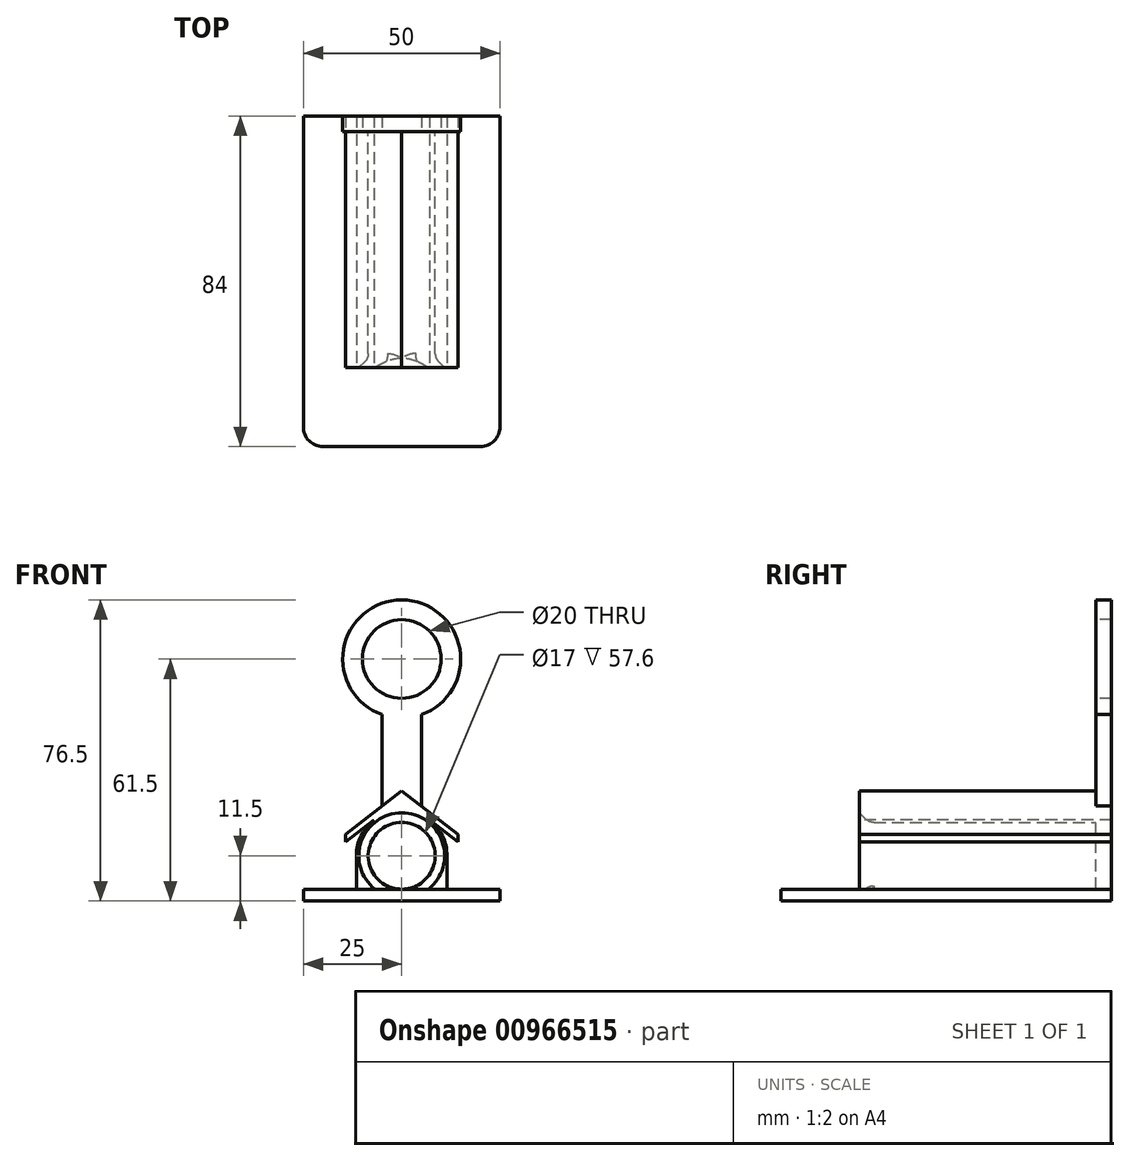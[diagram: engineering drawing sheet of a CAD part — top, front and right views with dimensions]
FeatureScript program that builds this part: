
annotation { "Feature Type Name" : "Feature", "Feature Type Description" : "" }
export const myFeature = defineFeature(function(context is Context, id is Id, definition is map)
    precondition{}
    {
        {
            var Q0;
            Q0=qCreatedBy(makeId("Front.planeOp"),FACE);
            var sketch = newSketch(context, id + "F0", { "sketchPlane" : qUnion([Q0])});
            skCircle(sketch, "E0", {"center": v(0, 0) * mm, "radius": 10 * mm});
            skCircle(sketch, "E1.0", {"center": v(0, 0) * mm, "radius": 15 * mm});
            skCircle(sketch, "E2", {"center": v(0, -50) * mm, "radius": 8.5 * mm});
            skLineSegment(sketch, "E3", {"start": v(0, -58.5) * mm, "end": v(25, -58.5) * mm});
            skLineSegment(sketch, "E4", {"start": v(25, -58.5) * mm, "end": v(25, -61.5) * mm});
            skLineSegment(sketch, "E5", {"start": v(25, -61.5) * mm, "end": v(0, -61.5) * mm});
            skLineSegment(sketch, "E6.MirrorCS", {"start": v(0, -58.5) * mm, "end": v(-25, -58.5) * mm});
            skLineSegment(sketch, "E7.MirrorCS", {"start": v(-25, -58.5) * mm, "end": v(-25, -61.5) * mm});
            skLineSegment(sketch, "E8.MirrorCS", {"start": v(-25, -61.5) * mm, "end": v(0, -61.5) * mm});
            skCircle(sketch, "E9.0", {"center": v(0, -50) * mm, "radius": 11.5 * mm});
            skLineSegment(sketch, "E10", {"start": v(11.5, -50) * mm, "end": v(11.5, -58.5) * mm});
            skLineSegment(sketch, "E11.MirrorCS", {"start": v(-11.5, -50) * mm, "end": v(-11.5, -58.5) * mm});
            skLineSegment(sketch, "E12", {"start": v(0, -35.5) * mm, "end": v(14.32, -46.5) * mm});
            skLineSegment(sketch, "E13", {"start": v(0, -33.5) * mm, "end": v(14.32, -44.5) * mm});
            skLineSegment(sketch, "E14", {"start": v(14.32, -44.5) * mm, "end": v(14.32, -46.5) * mm});
            skLineSegment(sketch, "E15.MirrorCS", {"start": v(0, -33.5) * mm, "end": v(-14.32, -44.5) * mm});
            skLineSegment(sketch, "E16.MirrorCS", {"start": v(0, -35.5) * mm, "end": v(-14.32, -46.5) * mm});
            skLineSegment(sketch, "E17.MirrorCS", {"start": v(-14.32, -44.5) * mm, "end": v(-14.32, -46.5) * mm});
            skLineSegment(sketch, "E18", {"start": v(5, -14.14) * mm, "end": v(5, -37.34) * mm});
            skLineSegment(sketch, "E19.MirrorCS", {"start": v(-5, -14.14) * mm, "end": v(-5, -37.34) * mm});
            skSolve(sketch);
        }
        {
            var Q0;
            Q0 = qSketchRegion(id + "F0", true);
            var Q1;
            Q1=makeQuery(id+"F0.imprint","IMPRINT",FACE,{"disambiguationData":[TD([[makeQuery(id+"F0.imprint","IMPRINT",EDGE,{"derivedFrom":sQuery(id+"F0.wireOp",EDGE,"E2")}),1.0]])]});
            extrude(context, id + "F1", {"entities" : qUnion([Q0, Q1]), "oppositeDirection" : true, "depth" : 4 * mm, "offsetDistance" : 25 * mm});
        }
        {
            var Q0;
            {var subQ0=sQuery(id+"F0.wireOp",EDGE,"E14");Q0=makeQuery(id+"F0.imprint","IMPRINT",FACE,{"disambiguationData":[TD([[makeQuery(id+"F0.imprint","IMPRINT",EDGE,{"derivedFrom":subQ0}),-1.0]])]});}
            var Q1;
            {var subQ0=sQuery(id+"F0.wireOp",EDGE,"E12");var subQ1=sQuery(id+"F0.wireOp",EDGE,"E9.0");var subQ2=makeQuery(id+"F0.imprint","INTERSECT",VERTEX,{"derivedFrom":[subQ1,subQ0]});Q1=makeQuery(id+"F0.imprint","IMPRINT",FACE,{"disambiguationData":[TD([[makeQuery(id+"F0.imprint","IMPRINT",EDGE,{"disambiguationData":[TD([[subQ2,-1.0]])],"derivedFrom":subQ1}),-1.0]])]});}
            var Q2;
            {var subQ3=sQuery(id+"F0.wireOp",EDGE,"E2");Q2=makeQuery(id+"F0.imprint","IMPRINT",FACE,{"disambiguationData":[TD([[makeQuery(id+"F0.imprint","IMPRINT",EDGE,{"derivedFrom":subQ3}),-1.0]])]});}
            var Q3;
            {var subQ1=sQuery(id+"F0.wireOp",EDGE,"E3");var subQ3=sQuery(id+"F0.wireOp",EDGE,"E9.0");var subQ4=makeQuery(id+"F0.imprint","INTERSECT",VERTEX,{"derivedFrom":[subQ1,subQ3]});Q3=makeQuery(id+"F0.imprint","IMPRINT",FACE,{"disambiguationData":[TD([[makeQuery(id+"F0.imprint","IMPRINT",EDGE,{"disambiguationData":[TD([[subQ4,1.0]])],"derivedFrom":subQ1}),-1.0]])]});}
            var Q4;
            {var subQ0=sQuery(id+"F0.wireOp",EDGE,"E10");Q4=makeQuery(id+"F0.imprint","IMPRINT",FACE,{"disambiguationData":[TD([[makeQuery(id+"F0.imprint","IMPRINT",EDGE,{"derivedFrom":subQ0}),-1.0]])]});}
            var Q5;
            {var subQ4=sQuery(id+"F0.wireOp",EDGE,"E4");Q5=makeQuery(id+"F0.imprint","IMPRINT",FACE,{"disambiguationData":[TD([[makeQuery(id+"F0.imprint","IMPRINT",EDGE,{"derivedFrom":subQ4}),-1.0]])]});}
            var Q6;
            {var subQ0=sQuery(id+"F0.wireOp",EDGE,"E11.MirrorCS");Q6=makeQuery(id+"F0.imprint","IMPRINT",FACE,{"disambiguationData":[TD([[makeQuery(id+"F0.imprint","IMPRINT",EDGE,{"derivedFrom":subQ0}),1.0]])]});}
            var Q7;
            {var subQ1=sQuery(id+"F0.wireOp",EDGE,"E7.MirrorCS");Q7=makeQuery(id+"F0.imprint","IMPRINT",FACE,{"disambiguationData":[TD([[makeQuery(id+"F0.imprint","IMPRINT",EDGE,{"derivedFrom":subQ1}),1.0]])]});}
            extrude(context, id + "F2", {"entities" : qUnion([Q0, Q1, Q2, Q3, Q4, Q5, Q6, Q7]), "operationType" : NewBodyOperationType.ADD, "depth" : 60 * mm, "offsetDistance" : 25 * mm});
        }
        {
            var Q0;
            {var subQ4=sQuery(id+"F0.wireOp",EDGE,"E4");Q0=makeQuery(id+"F0.imprint","IMPRINT",FACE,{"disambiguationData":[TD([[makeQuery(id+"F0.imprint","IMPRINT",EDGE,{"derivedFrom":subQ4}),-1.0]])]});}
            var Q1;
            {var subQ1=sQuery(id+"F0.wireOp",EDGE,"E3");var subQ3=sQuery(id+"F0.wireOp",EDGE,"E9.0");var subQ4=makeQuery(id+"F0.imprint","INTERSECT",VERTEX,{"derivedFrom":[subQ1,subQ3]});Q1=makeQuery(id+"F0.imprint","IMPRINT",FACE,{"disambiguationData":[TD([[makeQuery(id+"F0.imprint","IMPRINT",EDGE,{"disambiguationData":[TD([[subQ4,1.0]])],"derivedFrom":subQ1}),-1.0]])]});}
            var Q2;
            {var subQ1=sQuery(id+"F0.wireOp",EDGE,"E7.MirrorCS");Q2=makeQuery(id+"F0.imprint","IMPRINT",FACE,{"disambiguationData":[TD([[makeQuery(id+"F0.imprint","IMPRINT",EDGE,{"derivedFrom":subQ1}),1.0]])]});}
            extrude(context, id + "F3", {"entities" : qUnion([Q0, Q1, Q2]), "operationType" : NewBodyOperationType.ADD, "depth" : 80 * mm, "offsetDistance" : 25 * mm});
        }
        {
            var Q0;
            Q0=makeQuery(id+"F3.opExtrude","CAP_EDGE",EDGE,{"disambiguationData":[OSD([sQuery(id+"F0.wireOp",EDGE,"E4")])],"isStart":false});
            var Q1;
            Q1=makeQuery(id+"F3.opExtrude","CAP_EDGE",EDGE,{"disambiguationData":[OSD([sQuery(id+"F0.wireOp",EDGE,"E7.MirrorCS")])],"isStart":false});
            fillet(context, id + "F4", {"entities" : qUnion([Q0, Q1]), "radius" : 5 * mm, "tangentPropagation" : true, "allowEdgeOverflow" : false});
        }
        {
            var Q0;
            Q0=makeQuery(id+"F2.opExtrude","CAP_EDGE",EDGE,{"disambiguationData":[OSD([sQuery(id+"F0.wireOp",EDGE,"E2")])],"isStart":false});
            chamfer(context, id + "F5", {"entities" : qUnion([Q0]), "width" : 2.4 * mm, "tangentPropagation" : true});
        }
        {
            var Q0;
            {var subQ0=sQuery(id+"F0.wireOp",EDGE,"E2");Q0=makeQuery(id+"F5.opChamfer","BLEND_EDGE",EDGE,{"blendedFrom":[makeQuery(id+"F2.opExtrude","CAP_EDGE",EDGE,{"disambiguationData":[OSD([subQ0])],"isStart":false}),makeQuery(id+"F2.opExtrude","SWEPT_FACE",FACE,{"disambiguationData":[OSD([subQ0])]})],"blendedInto":[makeQuery(id+"F2.opExtrude","SWEPT_FACE",FACE,{"disambiguationData":[OSD([subQ0])]})]});}
            fillet(context, id + "F6", {"entities" : qUnion([Q0]), "radius" : 3 * mm, "tangentPropagation" : true, "allowEdgeOverflow" : false});
        }
    });
